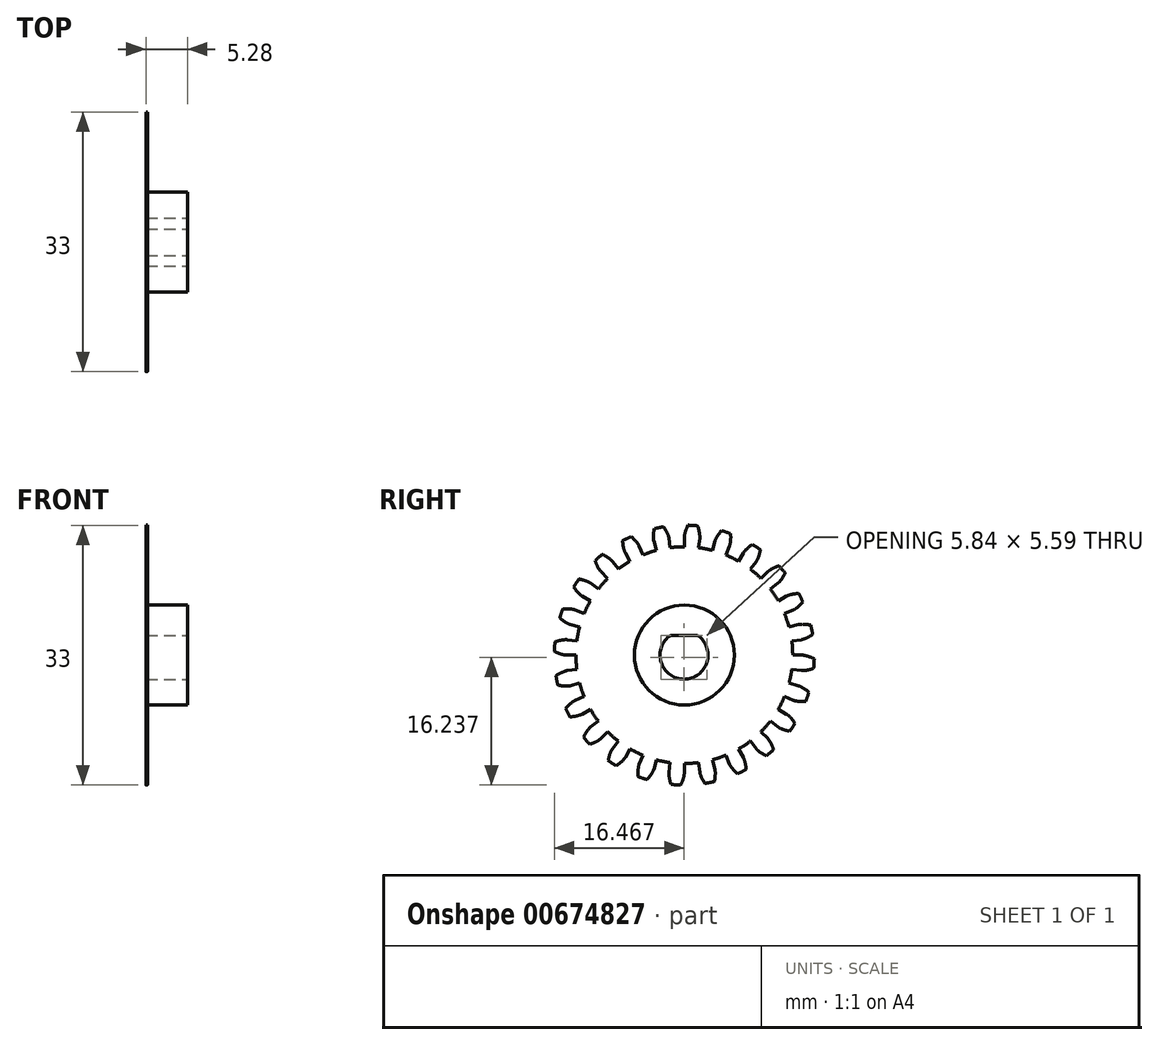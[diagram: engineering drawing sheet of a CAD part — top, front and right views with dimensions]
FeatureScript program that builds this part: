
annotation { "Feature Type Name" : "Feature", "Feature Type Description" : "" }
export const myFeature = defineFeature(function(context is Context, id is Id, definition is map)
    precondition{}
    {
        {
            assignVariable(context, id + "F0", {"name" : "NumberTeeth", "anyValue" : 24});
        }
        {
            assignVariable(context, id + "F1", {"name" : "GearThickness", "anyValue" : .2});
        }
        {
            var Q0;
            Q0=qCreatedBy(makeId("Right.planeOp"),FACE);
            var sketch = newSketch(context, id + "F2", { "sketchPlane" : qUnion([Q0])});
            skCircle(sketch, "E0", {"center": v(0, 0) * mm, "radius": 13.77 * mm});
            skCircle(sketch, "E1", {"center": v(0, 0) * mm, "radius": 15 * mm, "construction": true});
            skCircle(sketch, "E2", {"center": v(0, 0) * mm, "radius": 15.24 * mm, "construction": true});
            skCircle(sketch, "E3", {"center": v(0, 0) * mm, "radius": 16.51 * mm});
            skLineSegment(sketch, "E4", {"start": v(0, 0) * mm, "end": v(-15, 0) * mm, "construction": true});
            skLineSegment(sketch, "E5.1.0", {"start": v(0, 0) * mm, "end": v(-14.99, 0.75) * mm, "construction": true});
            skLineSegment(sketch, "E5.2.0", {"start": v(0, 0) * mm, "end": v(-14.93, 1.5) * mm, "construction": true});
            skLineSegment(sketch, "E5.3.0", {"start": v(0, 0) * mm, "end": v(-14.84, 2.24) * mm, "construction": true});
            skLineSegment(sketch, "E5.4.0", {"start": v(0, 0) * mm, "end": v(-14.7, 2.98) * mm, "construction": true});
            skLineSegment(sketch, "E5.5.0", {"start": v(0, 0) * mm, "end": v(-14.54, 3.71) * mm, "construction": true});
            skLineSegment(sketch, "E5.6.0", {"start": v(0, 0) * mm, "end": v(-14.34, 4.44) * mm, "construction": true});
            skLineSegment(sketch, "E5.7.0", {"start": v(0, 0) * mm, "end": v(-14.1, 5.15) * mm, "construction": true});
            skLineSegment(sketch, "E5.8.0", {"start": v(0, 0) * mm, "end": v(-13.82, 5.84) * mm, "construction": true});
            skLineSegment(sketch, "E5.9.0", {"start": v(0, 0) * mm, "end": v(-13.51, 6.53) * mm, "construction": true});
            skLineSegment(sketch, "E5.10.0", {"start": v(0, 0) * mm, "end": v(-13.17, 7.2) * mm, "construction": true});
            skLineSegment(sketch, "E5.11.0", {"start": v(0, 0) * mm, "end": v(-12.8, 7.84) * mm, "construction": true});
            skLineSegment(sketch, "E5.12.0", {"start": v(0, 0) * mm, "end": v(-12.39, 8.47) * mm, "construction": true});
            skLineSegment(sketch, "E5.13.0", {"start": v(0, 0) * mm, "end": v(-11.95, 9.08) * mm, "construction": true});
            skLineSegment(sketch, "E5.14.0", {"start": v(0, 0) * mm, "end": v(-11.48, 9.67) * mm, "construction": true});
            skLineSegment(sketch, "E5.anchor2", {"start": v(0, 0) * mm, "end": v(-11.48, 9.67) * mm, "construction": true});
            skLineSegment(sketch, "E6", {"start": v(-14.99, 0.75) * mm, "end": v(-15.03, 0) * mm, "construction": true});
            skLineSegment(sketch, "E7", {"start": v(-14.93, 1.5) * mm, "end": v(-15.08, 0) * mm, "construction": true});
            skLineSegment(sketch, "E8", {"start": v(-14.84, 2.24) * mm, "end": v(-15.18, 0.02) * mm, "construction": true});
            skLineSegment(sketch, "E9", {"start": v(-14.54, 3.71) * mm, "end": v(-15.47, 0.08) * mm, "construction": true});
            skLineSegment(sketch, "E10", {"start": v(-14.34, 4.44) * mm, "end": v(-15.67, 0.13) * mm, "construction": true});
            skLineSegment(sketch, "E11", {"start": v(-14.1, 5.15) * mm, "end": v(-15.9, 0.21) * mm, "construction": true});
            skLineSegment(sketch, "E12", {"start": v(-13.82, 5.84) * mm, "end": v(-16.16, 0.32) * mm, "construction": true});
            skLineSegment(sketch, "E13", {"start": v(-13.51, 6.53) * mm, "end": v(-16.45, 0.45) * mm, "construction": true});
            skLineSegment(sketch, "E14", {"start": v(-13.17, 7.2) * mm, "end": v(-16.77, 0.6) * mm, "construction": true});
            skLineSegment(sketch, "E15", {"start": v(-12.8, 7.84) * mm, "end": v(-17.1, 0.8) * mm, "construction": true});
            skLineSegment(sketch, "E16", {"start": v(-14.7, 2.98) * mm, "end": v(-15.3, 0.04) * mm, "construction": true});
            skLineSegment(sketch, "E17", {"start": v(-12.39, 8.47) * mm, "end": v(-17.47, 1.04) * mm, "construction": true});
            skLineSegment(sketch, "E18", {"start": v(-11.95, 9.08) * mm, "end": v(-17.85, 1.32) * mm, "construction": true});
            skLineSegment(sketch, "E19", {"start": v(-11.48, 9.67) * mm, "end": v(-18.25, 1.63) * mm, "construction": true});
            skLineSegment(sketch, "E20", {"start": v(0, 0) * mm, "end": v(-14.98, 0.98) * mm, "construction": true});
            skLineSegment(sketch, "E21", {"start": v(-13.77, 0) * mm, "end": v(-15, 0) * mm});
            skLineSegment(sketch, "E22.MirrorCS", {"start": v(-13.65, 1.8) * mm, "end": v(-14.88, 1.96) * mm});
            skFitSpline(sketch, "E23", {"points": [v(-15, 0) * mm, v(-15.03, 0) * mm, v(-15.08, 0) * mm, v(-15.18, 0.02) * mm, v(-15.3, 0.04) * mm, v(-15.47, 0.08) * mm, v(-15.67, 0.13) * mm, v(-15.9, 0.21) * mm, v(-16.16, 0.32) * mm, v(-16.45, 0.45) * mm, v(-16.77, 0.6) * mm, v(-17.1, 0.8) * mm, v(-17.47, 1.04) * mm, v(-17.85, 1.32) * mm, v(-18.25, 1.63) * mm], "startDerivative": vector(-0.82, 0) * mm, "endDerivative": vector(-1.19, 1) * mm});
            skLineSegment(sketch, "E24", {"start": v(-18.25, 1.63) * mm, "end": v(-18.88, 2.16) * mm, "construction": true});
            skFitSpline(sketch, "E25.MirrorCS", {"points": [v(-14.88, 1.96) * mm, v(-14.9, 1.96) * mm, v(-14.95, 1.96) * mm, v(-15.05, 1.96) * mm, v(-15.18, 1.96) * mm, v(-15.35, 1.94) * mm, v(-15.55, 1.91) * mm, v(-15.8, 1.87) * mm, v(-16.06, 1.8) * mm, v(-16.37, 1.7) * mm, v(-16.7, 1.58) * mm, v(-17.07, 1.43) * mm, v(-17.46, 1.25) * mm, v(-17.87, 1.02) * mm, v(-18.3, 0.76) * mm], "startDerivative": vector(-0.81, 0.1) * mm, "endDerivative": vector(-1.3, -0.84) * mm});
            skSolve(sketch);
        }
        {
            var Q0;
            {var subQ0=sQuery(id+"F2.wireOp",EDGE,"E0");var subQ27=makeQuery(id+"F2.imprint","INTERSECT",VERTEX,{"derivedFrom":[subQ0,sQuery(id+"F2.wireOp",EDGE,"10ea1024-8cf5-41f5-a75f-a634b86921f3.10.0")]});Q0=makeQuery(id+"F2.imprint","IMPRINT",FACE,{"disambiguationData":[TD([[makeQuery(id+"F2.imprint","IMPRINT",EDGE,{"disambiguationData":[TD([[subQ27,-1.0]])],"derivedFrom":subQ0}),1.0]])]});}
            var Q1;
            {var subQ0=sQuery(id+"F2.wireOp",EDGE,"10ea1024-8cf5-41f5-a75f-a634b86921f3.1.0");Q1=makeQuery(id+"F2.imprint","IMPRINT",FACE,{"disambiguationData":[TD([[makeQuery(id+"F2.imprint","IMPRINT",EDGE,{"derivedFrom":subQ0}),-1.0]])]});}
            var Q2;
            {var subQ7=sQuery(id+"F2.wireOp",EDGE,"10ea1024-8cf5-41f5-a75f-a634b86921f3.2.0");Q2=makeQuery(id+"F2.imprint","IMPRINT",FACE,{"disambiguationData":[TD([[makeQuery(id+"F2.imprint","IMPRINT",EDGE,{"derivedFrom":subQ7}),-1.0]])]});}
            var Q3;
            {var subQ8=sQuery(id+"F2.wireOp",EDGE,"10ea1024-8cf5-41f5-a75f-a634b86921f3.3.0");Q3=makeQuery(id+"F2.imprint","IMPRINT",FACE,{"disambiguationData":[TD([[makeQuery(id+"F2.imprint","IMPRINT",EDGE,{"derivedFrom":subQ8}),-1.0]])]});}
            var Q4;
            {var subQ2=sQuery(id+"F2.wireOp",EDGE,"10ea1024-8cf5-41f5-a75f-a634b86921f3.4.0");Q4=makeQuery(id+"F2.imprint","IMPRINT",FACE,{"disambiguationData":[TD([[makeQuery(id+"F2.imprint","IMPRINT",EDGE,{"derivedFrom":subQ2}),-1.0]])]});}
            var Q5;
            {var subQ8=sQuery(id+"F2.wireOp",EDGE,"10ea1024-8cf5-41f5-a75f-a634b86921f3.5.0");Q5=makeQuery(id+"F2.imprint","IMPRINT",FACE,{"disambiguationData":[TD([[makeQuery(id+"F2.imprint","IMPRINT",EDGE,{"derivedFrom":subQ8}),-1.0]])]});}
            var Q6;
            {var subQ3=sQuery(id+"F2.wireOp",EDGE,"10ea1024-8cf5-41f5-a75f-a634b86921f3.6.0");Q6=makeQuery(id+"F2.imprint","IMPRINT",FACE,{"disambiguationData":[TD([[makeQuery(id+"F2.imprint","IMPRINT",EDGE,{"derivedFrom":subQ3}),-1.0]])]});}
            var Q7;
            {var subQ0=sQuery(id+"F2.wireOp",EDGE,"10ea1024-8cf5-41f5-a75f-a634b86921f3.7.0");Q7=makeQuery(id+"F2.imprint","IMPRINT",FACE,{"disambiguationData":[TD([[makeQuery(id+"F2.imprint","IMPRINT",EDGE,{"derivedFrom":subQ0}),-1.0]])]});}
            var Q8;
            {var subQ5=sQuery(id+"F2.wireOp",EDGE,"10ea1024-8cf5-41f5-a75f-a634b86921f3.8.0");Q8=makeQuery(id+"F2.imprint","IMPRINT",FACE,{"disambiguationData":[TD([[makeQuery(id+"F2.imprint","IMPRINT",EDGE,{"derivedFrom":subQ5}),-1.0]])]});}
            var Q9;
            {var subQ1=sQuery(id+"F2.wireOp",EDGE,"10ea1024-8cf5-41f5-a75f-a634b86921f3.9.0");Q9=makeQuery(id+"F2.imprint","IMPRINT",FACE,{"disambiguationData":[TD([[makeQuery(id+"F2.imprint","IMPRINT",EDGE,{"derivedFrom":subQ1}),-1.0]])]});}
            var Q10;
            {var subQ5=sQuery(id+"F2.wireOp",EDGE,"10ea1024-8cf5-41f5-a75f-a634b86921f3.10.0");Q10=makeQuery(id+"F2.imprint","IMPRINT",FACE,{"disambiguationData":[TD([[makeQuery(id+"F2.imprint","IMPRINT",EDGE,{"derivedFrom":subQ5}),-1.0]])]});}
            var Q11;
            {var subQ8=sQuery(id+"F2.wireOp",EDGE,"10ea1024-8cf5-41f5-a75f-a634b86921f3.11.0");Q11=makeQuery(id+"F2.imprint","IMPRINT",FACE,{"disambiguationData":[TD([[makeQuery(id+"F2.imprint","IMPRINT",EDGE,{"derivedFrom":subQ8}),-1.0]])]});}
            var Q12;
            {var subQ2=sQuery(id+"F2.wireOp",EDGE,"10ea1024-8cf5-41f5-a75f-a634b86921f3.12.0");Q12=makeQuery(id+"F2.imprint","IMPRINT",FACE,{"disambiguationData":[TD([[makeQuery(id+"F2.imprint","IMPRINT",EDGE,{"derivedFrom":subQ2}),-1.0]])]});}
            var Q13;
            {var subQ3=sQuery(id+"F2.wireOp",EDGE,"10ea1024-8cf5-41f5-a75f-a634b86921f3.13.0");Q13=makeQuery(id+"F2.imprint","IMPRINT",FACE,{"disambiguationData":[TD([[makeQuery(id+"F2.imprint","IMPRINT",EDGE,{"derivedFrom":subQ3}),-1.0]])]});}
            var Q14;
            {var subQ0=sQuery(id+"F2.wireOp",EDGE,"10ea1024-8cf5-41f5-a75f-a634b86921f3.14.0");Q14=makeQuery(id+"F2.imprint","IMPRINT",FACE,{"disambiguationData":[TD([[makeQuery(id+"F2.imprint","IMPRINT",EDGE,{"derivedFrom":subQ0}),-1.0]])]});}
            var Q15;
            {var subQ6=sQuery(id+"F2.wireOp",EDGE,"10ea1024-8cf5-41f5-a75f-a634b86921f3.15.0");Q15=makeQuery(id+"F2.imprint","IMPRINT",FACE,{"disambiguationData":[TD([[makeQuery(id+"F2.imprint","IMPRINT",EDGE,{"derivedFrom":subQ6}),-1.0]])]});}
            var Q16;
            {var subQ5=sQuery(id+"F2.wireOp",EDGE,"10ea1024-8cf5-41f5-a75f-a634b86921f3.16.0");Q16=makeQuery(id+"F2.imprint","IMPRINT",FACE,{"disambiguationData":[TD([[makeQuery(id+"F2.imprint","IMPRINT",EDGE,{"derivedFrom":subQ5}),-1.0]])]});}
            var Q17;
            {var subQ7=sQuery(id+"F2.wireOp",EDGE,"10ea1024-8cf5-41f5-a75f-a634b86921f3.17.0");Q17=makeQuery(id+"F2.imprint","IMPRINT",FACE,{"disambiguationData":[TD([[makeQuery(id+"F2.imprint","IMPRINT",EDGE,{"derivedFrom":subQ7}),-1.0]])]});}
            var Q18;
            {var subQ5=sQuery(id+"F2.wireOp",EDGE,"10ea1024-8cf5-41f5-a75f-a634b86921f3.18.0");Q18=makeQuery(id+"F2.imprint","IMPRINT",FACE,{"disambiguationData":[TD([[makeQuery(id+"F2.imprint","IMPRINT",EDGE,{"derivedFrom":subQ5}),-1.0]])]});}
            var Q19;
            {var subQ8=sQuery(id+"F2.wireOp",EDGE,"10ea1024-8cf5-41f5-a75f-a634b86921f3.19.0");Q19=makeQuery(id+"F2.imprint","IMPRINT",FACE,{"disambiguationData":[TD([[makeQuery(id+"F2.imprint","IMPRINT",EDGE,{"derivedFrom":subQ8}),-1.0]])]});}
            var Q20;
            {var subQ8=sQuery(id+"F2.wireOp",EDGE,"E21");Q20=makeQuery(id+"F2.imprint","IMPRINT",FACE,{"disambiguationData":[TD([[makeQuery(id+"F2.imprint","IMPRINT",EDGE,{"derivedFrom":subQ8}),-1.0]])]});}
            extrude(context, id + "F3", {"entities" : qUnion([Q0, Q1, Q2, Q3, Q4, Q5, Q6, Q7, Q8, Q9, Q10, Q11, Q12, Q13, Q14, Q15, Q16, Q17, Q18, Q19, Q20]), "depth" : (getVariable(context, 'GearThickness')) * mm});
        }
        {
            var Q0;
            Q0=makeQuery(id+"F3.opExtrude","SWEPT_FACE",FACE,{"disambiguationData":[OSD([sQuery(id+"F2.wireOp",EDGE,"E25.MirrorCS")])]});
            var Q1;
            Q1=makeQuery(id+"F3.opExtrude","SWEPT_FACE",FACE,{"disambiguationData":[OSD([sQuery(id+"F2.wireOp",EDGE,"E23")])]});
            var Q2;
            Q2=makeQuery(id+"F3.opExtrude","SWEPT_FACE",FACE,{"disambiguationData":[OSD([sQuery(id+"F2.wireOp",EDGE,"E3")])]});
            var Q3;
            Q3=makeQuery(id+"F3.opExtrude","SWEPT_FACE",FACE,{"disambiguationData":[OSD([sQuery(id+"F2.wireOp",EDGE,"E22.MirrorCS")])]});
            var Q4;
            Q4=makeQuery(id+"F3.opExtrude","SWEPT_FACE",FACE,{"disambiguationData":[OSD([sQuery(id+"F2.wireOp",EDGE,"E21")])]});
            var Q5;
            Q5=makeQuery(id+"F3.opExtrude","SWEPT_FACE",FACE,{"disambiguationData":[OSD([sQuery(id+"F2.wireOp",EDGE,"E0")])]});
            circularPattern(context, id + "F4", {"faces" : qUnion([Q0, Q1, Q2, Q3, Q4]), "axis" : qUnion([Q5]), "angle" : 360 * degree, "instanceCount" : getVariable(context, 'NumberTeeth'), "equalSpace" : true, "patternType" : PatternType.FACE});
        }
        {
            var Q0;
            Q0=makeQuery(id+"F3.opExtrude","CAP_FACE",FACE,{"disambiguationData":[OSD([sQuery(id+"F2.wireOp",EDGE,"E0"),sQuery(id+"F2.wireOp",EDGE,"E3"),sQuery(id+"F2.wireOp",EDGE,"E21"),sQuery(id+"F2.wireOp",EDGE,"E22.MirrorCS"),sQuery(id+"F2.wireOp",EDGE,"E23"),sQuery(id+"F2.wireOp",EDGE,"E25.MirrorCS")])],"isStart":false});
            var sketch = newSketch(context, id + "F5", { "sketchPlane" : qUnion([Q0])});
            skArc(sketch, "E26", {"start": v(-1.72, 2.53) * mm, "mid": v(-0.03, -3.06) * mm, "end": v(1.65, 2.53) * mm});
            skPoint(sketch, "E27.middle", {"position": v(0, 0) * mm});
            skLineSegment(sketch, "E28", {"start": v(1.65, 2.53) * mm, "end": v(-1.72, 2.53) * mm});
            skCircle(sketch, "E29", {"center": v(0, 0) * mm, "radius": 6.35 * mm});
            skSolve(sketch);
        }
        {
            var Q0;
            Q0=makeQuery(id+"F5.imprint","IMPRINT",FACE,{"disambiguationData":[TD([[makeQuery(id+"F5.imprint","IMPRINT",EDGE,{"derivedFrom":sQuery(id+"F5.wireOp",EDGE,"E26")}),1.0]])]});
            extrude(context, id + "F6", {"entities" : qUnion([Q0]), "operationType" : NewBodyOperationType.REMOVE, "oppositeDirection" : true, "depth" : 25.4 * mm, "offsetDistance" : 25.4 * mm});
        }
        {
            var Q0;
            Q0=makeQuery(id+"F5.imprint","IMPRINT",FACE,{"disambiguationData":[TD([[makeQuery(id+"F5.imprint","IMPRINT",EDGE,{"derivedFrom":sQuery(id+"F5.wireOp",EDGE,"E26")}),-1.0]])]});
            extrude(context, id + "F7", {"entities" : qUnion([Q0]), "operationType" : NewBodyOperationType.ADD, "depth" : 5.08 * mm, "offsetDistance" : 25.4 * mm});
        }
    });
